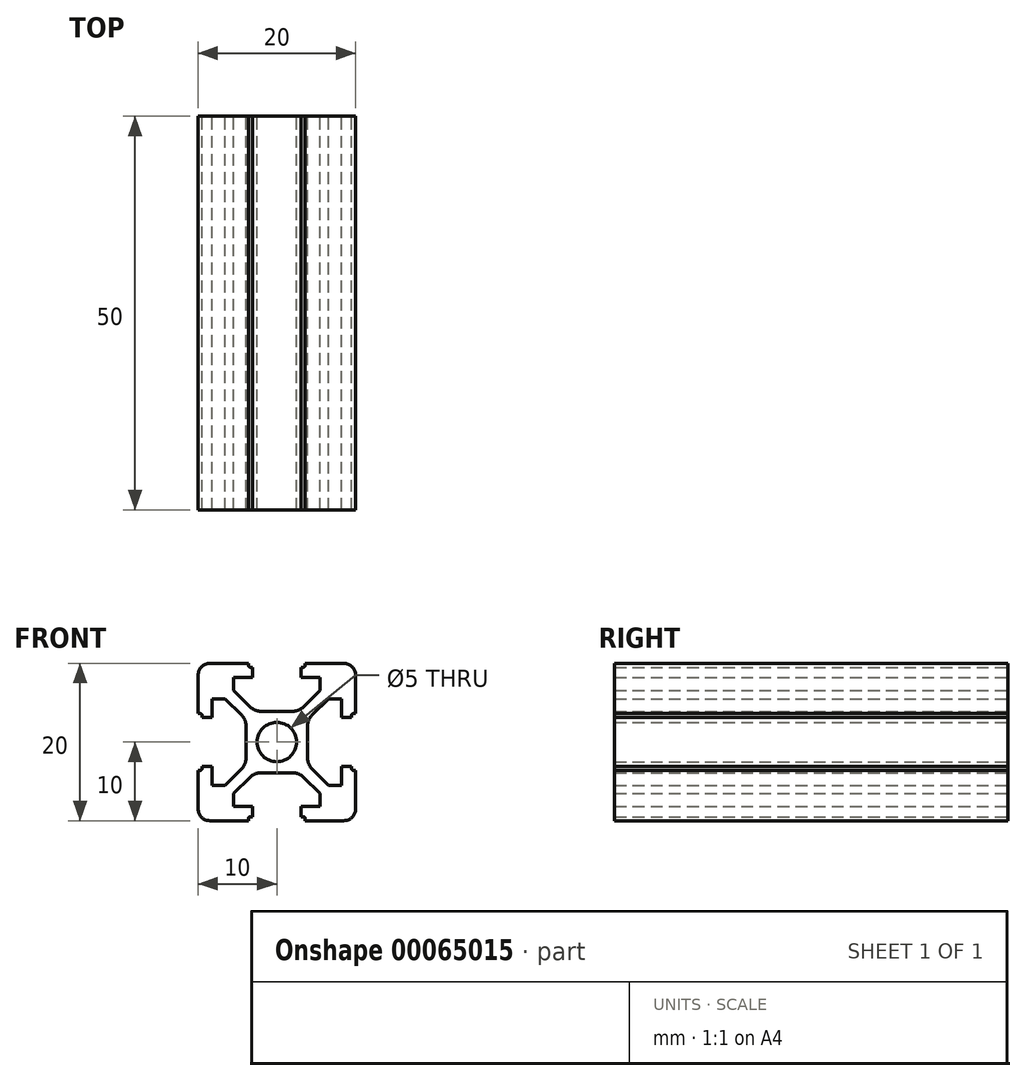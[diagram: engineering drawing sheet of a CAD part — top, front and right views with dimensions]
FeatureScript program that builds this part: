
annotation { "Feature Type Name" : "Feature", "Feature Type Description" : "" }
export const myFeature = defineFeature(function(context is Context, id is Id, definition is map)
    precondition{}
    {
        {
            var Q0;
            Q0=qCreatedBy(makeId("Front.planeOp"),FACE);
            var sketch = newSketch(context, id + "F0", { "sketchPlane" : qUnion([Q0])});
            skLineSegment(sketch, "E0", {"start": v(-10, 3.6) * mm, "end": v(-10, 8.5) * mm});
            skLineSegment(sketch, "E1", {"start": v(-8.5, 10) * mm, "end": v(-3.6, 10) * mm});
            skLineSegment(sketch, "E2", {"start": v(-3.6, 10) * mm, "end": v(-3.6, 9.7) * mm});
            skLineSegment(sketch, "E3", {"start": v(-3.4, 9.5) * mm, "end": v(-3.1, 9.5) * mm});
            skLineSegment(sketch, "E4", {"start": v(-3.1, 9.5) * mm, "end": v(-3.1, 8.2) * mm});
            skLineSegment(sketch, "E5", {"start": v(-3.1, 8.2) * mm, "end": v(-5.5, 8.2) * mm});
            skLineSegment(sketch, "E6", {"start": v(-5.5, 8.2) * mm, "end": v(-5.5, 6.56) * mm});
            skLineSegment(sketch, "E7", {"start": v(-5.5, 6.56) * mm, "end": v(-3.43, 4.49) * mm});
            skLineSegment(sketch, "E8", {"start": v(-2.01, 3.9) * mm, "end": v(0, 3.9) * mm});
            skLineSegment(sketch, "E9", {"start": v(0, 3.9) * mm, "end": v(0, 2.5) * mm});
            skLineSegment(sketch, "E10", {"start": v(-2.5, 0) * mm, "end": v(-3.9, 0) * mm});
            skLineSegment(sketch, "E11", {"start": v(-3.9, 0) * mm, "end": v(-3.9, 2.01) * mm});
            skLineSegment(sketch, "E12", {"start": v(-4.49, 3.43) * mm, "end": v(-6.56, 5.5) * mm});
            skLineSegment(sketch, "E13", {"start": v(-6.56, 5.5) * mm, "end": v(-8.2, 5.5) * mm});
            skLineSegment(sketch, "E14", {"start": v(-8.2, 5.5) * mm, "end": v(-8.2, 3.1) * mm});
            skLineSegment(sketch, "E15", {"start": v(-8.2, 3.1) * mm, "end": v(-9.5, 3.1) * mm});
            skLineSegment(sketch, "E16", {"start": v(-9.5, 3.1) * mm, "end": v(-9.5, 3.4) * mm});
            skLineSegment(sketch, "E17", {"start": v(-9.7, 3.6) * mm, "end": v(-10, 3.6) * mm});
            skLineSegment(sketch, "E18", {"start": v(-10, 10) * mm, "end": v(0, 0) * mm, "construction": true});
            skArc(sketch, "E19", {"start": v(0, 2.5) * mm, "mid": v(-1.77, 1.77) * mm, "end": v(-2.5, 0) * mm});
            skPoint(sketch, "E20.visualSharp", {"position": v(-10, 10) * mm});
            skArc(sketch, "E20.filletArc", {"start": v(-8.5, 10) * mm, "mid": v(-9.56, 9.56) * mm, "end": v(-10, 8.5) * mm});
            skPoint(sketch, "E21.visualSharp", {"position": v(-3.9, 2.84) * mm});
            skArc(sketch, "E21.filletArc", {"start": v(-3.9, 2.01) * mm, "mid": v(-4.05, 2.78) * mm, "end": v(-4.49, 3.43) * mm});
            skPoint(sketch, "E22.visualSharp", {"position": v(-2.84, 3.9) * mm});
            skArc(sketch, "E22.filletArc", {"start": v(-3.43, 4.49) * mm, "mid": v(-2.78, 4.05) * mm, "end": v(-2.01, 3.9) * mm});
            skPoint(sketch, "E23.visualSharp", {"position": v(-3.6, 9.5) * mm});
            skArc(sketch, "E23.filletArc", {"start": v(-3.6, 9.7) * mm, "mid": v(-3.54, 9.56) * mm, "end": v(-3.4, 9.5) * mm});
            skPoint(sketch, "E24.visualSharp", {"position": v(-9.5, 3.6) * mm});
            skArc(sketch, "E24.filletArc", {"start": v(-9.5, 3.4) * mm, "mid": v(-9.56, 3.54) * mm, "end": v(-9.7, 3.6) * mm});
            skSolve(sketch);
        }
        {
            var Q0;
            Q0=makeQuery(id+"F0.imprint","IMPRINT",FACE,{"disambiguationData":[TD([[makeQuery(id+"F0.imprint","IMPRINT",EDGE,{"derivedFrom":sQuery(id+"F0.wireOp",EDGE,"E0")}),-1.0]])]});
            extrude(context, id + "F1", {"entities" : qUnion([Q0]), "depth" : 25 * mm, "hasSecondDirection" : true, "secondDirectionOppositeDirection" : true, "secondDirectionDepth" : 25 * mm, "offsetDistance" : 25 * mm});
        }
        {
            var Q0;
            Q0=qCreatedBy(makeId("Right.planeOp"),FACE);
            var sketch = newSketch(context, id + "F2", { "sketchPlane" : qUnion([Q0])});
            skLineSegment(sketch, "E25", {"start": v(0, 0) * mm, "end": v(-25, 0) * mm, "construction": true});
            skSolve(sketch);
        }
        {
            var Q0;
            Q0=makeQuery(id+"F1.opExtrude","SWEPT_BODY",BODY,{"disambiguationData":[OSD([sQuery(id+"F0.wireOp",EDGE,"E0"),sQuery(id+"F0.wireOp",EDGE,"E1"),sQuery(id+"F0.wireOp",EDGE,"E2"),sQuery(id+"F0.wireOp",EDGE,"E3"),sQuery(id+"F0.wireOp",EDGE,"E4"),sQuery(id+"F0.wireOp",EDGE,"E5"),sQuery(id+"F0.wireOp",EDGE,"E6"),sQuery(id+"F0.wireOp",EDGE,"E7"),sQuery(id+"F0.wireOp",EDGE,"E8"),sQuery(id+"F0.wireOp",EDGE,"E9"),sQuery(id+"F0.wireOp",EDGE,"E10"),sQuery(id+"F0.wireOp",EDGE,"E11"),sQuery(id+"F0.wireOp",EDGE,"E12"),sQuery(id+"F0.wireOp",EDGE,"E13"),sQuery(id+"F0.wireOp",EDGE,"E14"),sQuery(id+"F0.wireOp",EDGE,"E15"),sQuery(id+"F0.wireOp",EDGE,"E16"),sQuery(id+"F0.wireOp",EDGE,"E17"),sQuery(id+"F0.wireOp",EDGE,"E19"),sQuery(id+"F0.wireOp",EDGE,"E20.filletArc"),sQuery(id+"F0.wireOp",EDGE,"E21.filletArc"),sQuery(id+"F0.wireOp",EDGE,"E22.filletArc"),sQuery(id+"F0.wireOp",EDGE,"E23.filletArc"),sQuery(id+"F0.wireOp",EDGE,"E24.filletArc")])]});
            var Q1;
            Q1=sQuery(id+"F2.wireOp",EDGE,"E25");
            circularPattern(context, id + "F3", {"operationType" : NewBodyOperationType.ADD, "entities" : qUnion([Q0]), "axis" : qUnion([Q1]), "angle" : 360 * degree, "instanceCount" : 4, "equalSpace" : true});
        }
    });
